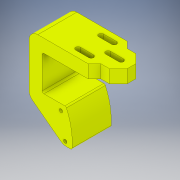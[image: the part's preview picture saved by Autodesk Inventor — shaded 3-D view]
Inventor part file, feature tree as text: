
AUTODESK INVENTOR PART (.ipt)
format: ipt  version: 2019 (Build 230136000, 136)  size: 472,576 bytes
history: native  units: in
note: dims shown in document units (in); Inventor stores cm internally (conversion verified against a paired STEP export)
features: extrude x20, sketch x18, mirror x2, fillet x2, loft x1, hole x1, other x1
ambient origin geometry x8: Origin, YZ Plane, XZ Plane, XY Plane, X Axis, Y Axis, Z Axis, Center Point
bodies: Solid1 (feature_tree)
feature tree (45):
  sketch  "Sketch1"  dims[d0=0.5497in d1=0.3937in]
  sketch  "Sketch2"  dims[d2=0.3937in d3=0.3937in]
  extrude  "Extrusion1"  Depth=0.3937in
  extrude  "Extrusion2"  Depth=0.3937in
  sketch  "Sketch3"  dims[d4=3.937in d5=0.7874in]
  extrude  "Extrusion3"  Depth=0.7874in
  extrude  "Extrusion5"  Depth=0.3937in
  extrude  "Extrusion6"  Depth=1.1811in
  extrude  "Extrusion7"  Depth=0.3937in TaperAngle=0.0deg
  extrude  "Extrusion9"  Depth=1.1811in TaperAngle=0.0deg
  loft  "Loft1"
  mirror  "Mirror2"
  extrude  "Extrusion10"  Depth=0.3937in
  extrude  "Extrusion11"  Depth=1.9685in TaperAngle=0.0deg
  sketch  "Sketch12"  dims[d28=0.1181in d29=1.9685in d30=0.0in]
  extrude  "Extrusion12"  Depth=0.9843in
  extrude  "Extrusion15"  Depth=0.2749in
  extrude  "Extrusion17"  Depth=0.1374in
  sketch  "Sketch17"  dims[d40=0.2749in d41=1.378in]
  extrude  "Extrusion18"  Depth=1.378in
  extrude  "Extrusion16"  Depth=1.5748in
  extrude  "Extrusion13"  Depth=1.5748in
  sketch  "Sketch14"  dims[d36=0.1374in d37=0.2749in]
  hole  "Hole3"  [1 undecoded]
  extrude  "Extrusion14"  Depth=1.5748in
  extrude  "Extrusion19"  Depth=1.5748in
  extrude  "Extrusion20"  Depth=1.5748in
  extrude  "Extrusion21"  Depth=1.5748in TaperAngle=0.0deg
  fillet  "Fillet1"  Radius=0.3268in
  fillet  "Fillet2"  Radius=0.3268in
  extrude  "Extrusion22"  Depth=1.5748in
  mirror  "Mirror3"
  sketch  "Sketch5"  dims[d6=0.3937in d7=2.7559in]
  sketch  "Sketch6"  dims[d8=75.0deg d9=1.1811in]
  sketch  "Sketch8"  dims[d10=0.3937in d13=3.937in d14=0.0in]
  sketch  "Sketch9"  dims[d15=1.1811in d16=0.0in d17=1.1811in d18=2.3622in d19=0.0in d20=0.0in]
  other  "Edges1"
  sketch  "Sketch10"  dims[d23=1.1811in d24=0.3937in d25=0.0in]
  sketch  "Sketch11"  dims[d26=0.7874in d27=0.3937in]
  sketch  "Sketch13"  dims[d31=0.2047in d35=0.9843in]
  sketch  "Sketch15"  dims[d38=1.189in d39=0.1374in]
  sketch  "Sketch18"  dims[d42=1.5748in d43=0.0in d49=0.3622in]
  sketch  "Sketch19"  dims[d50=1.5748in d51=0.0in d53=0.315in]
  sketch  "Sketch20"  dims[d54=0.0in d55=90.0deg d56=0.0in d57=90.0deg d58=0.315in]
  sketch  "Sketch21"  dims[d59=0.3937in d60=0.0in d61=2.478in d62=0.3268in d63=0.3268in d64=0.1181in d65=0.0in d66=0.3268in d67=0.3268in d68=0.3543in d69=0.2362in d70=0.0in d85=0.2205in d86=1.1811in d87=0.0in d88=0.3307in d89=1.1811in d90=0.2362in d91=0.0in d92=0.2047in d93=0.2362in d94=0.1575in d95=0.0787in d96=90.0deg d97=0.1969in d98=0.8108in d99=0.0787in d100=0.2362in d101=0.0in d102=0.2205in d103=0.2205in d104=3.937in d105=0.3937in d106=0.0in d107=0.0in d108=1.1811in d109=3.937in d110=0.0in d116=0.5906in d117=0.0in d118=5.9055in d119=0.0in d120=0.9843in d125=0.3937in d126=0.5906in d127=0.3937in d128=1.5748in d129=0.3937in d130=0.0in d131=0.3937in d132=0.1969in d133=0.1969in d134=0.315in d135=0.315in d136=45.0deg d137=45.0deg d138=135.0deg d139=135.0deg d140=0.3937in d141=1.1811in d142=0.5906in d143=0.0in d144=0.0in d145=0.0in d146=0.3937in d147=0.0787in d149=30.0deg d150=0.5118in d151=0.1575in d152=0.1575in d153=0.315in d154=0.1969in d155=0.2756in d156=0.1969in d157=0.0in d158=1.5748in]
note: 1 required parameter value undecoded (feature->parameter linkage not recoverable at this tier; creation-order binding heuristic only, values carry confidence <= 0.55)
